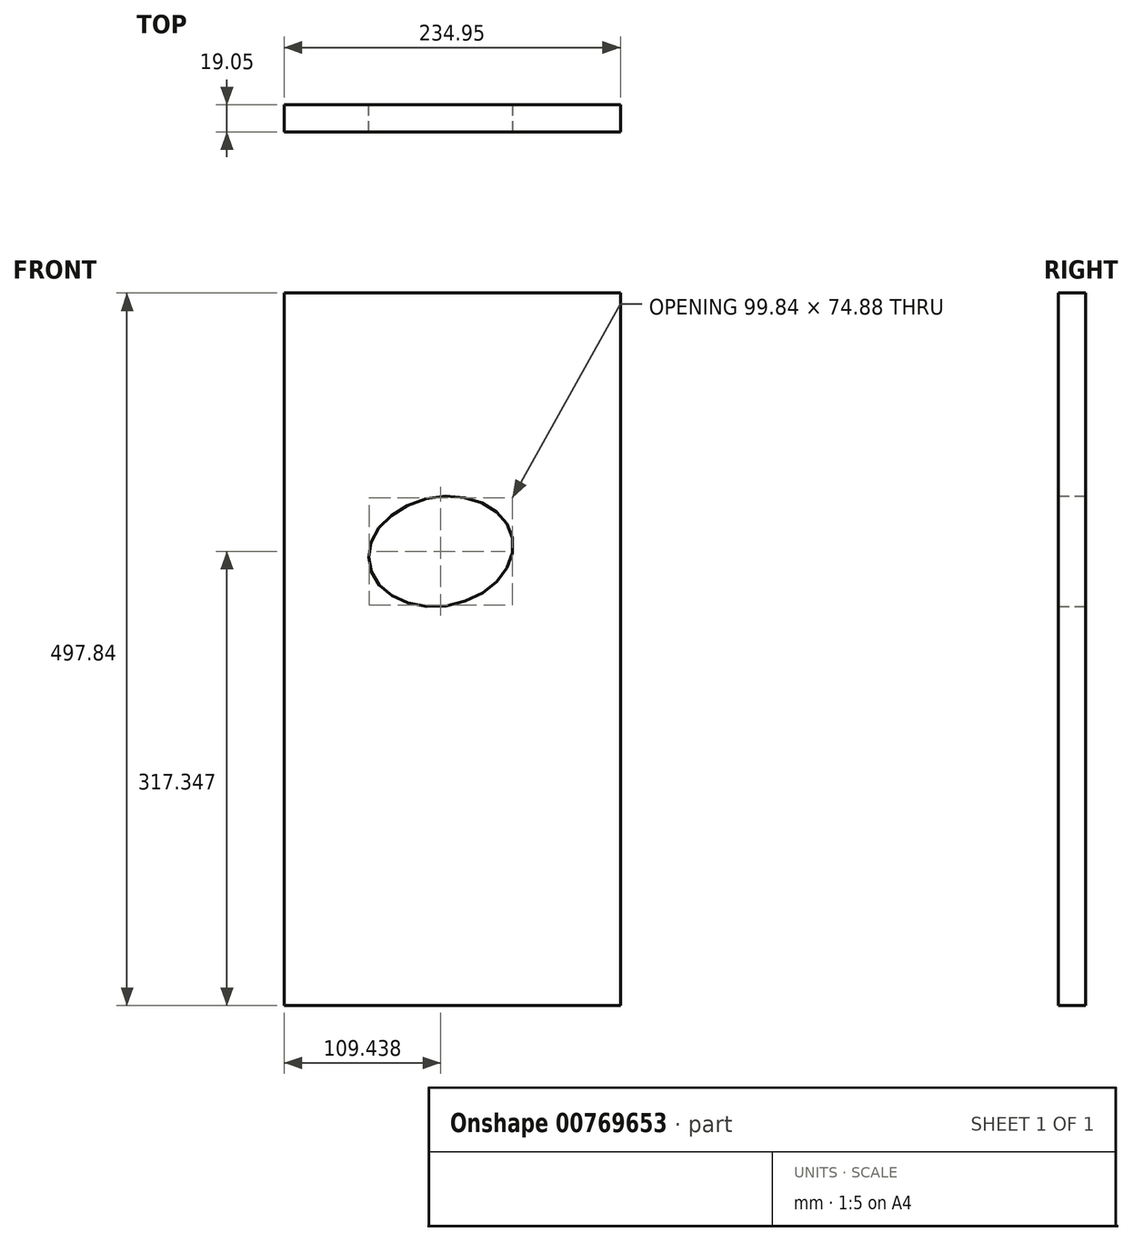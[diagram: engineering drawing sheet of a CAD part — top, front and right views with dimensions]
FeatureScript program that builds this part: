
annotation { "Feature Type Name" : "Feature", "Feature Type Description" : "" }
export const myFeature = defineFeature(function(context is Context, id is Id, definition is map)
    precondition{}
    {
        {
            var Q0;
            Q0=qCreatedBy(makeId("Front.planeOp"),FACE);
            var sketch = newSketch(context, id + "F0", { "sketchPlane" : qUnion([Q0])});
            skLineSegment(sketch, "E0.bottom", {"start": v(-193.54, 428.98) * mm, "end": v(41.41, 428.98) * mm});
            skLineSegment(sketch, "E0.top", {"start": v(-193.54, -68.86) * mm, "end": v(41.41, -68.86) * mm});
            skLineSegment(sketch, "E0.left", {"start": v(-193.54, 428.98) * mm, "end": v(-193.54, -68.86) * mm});
            skLineSegment(sketch, "E0.right", {"start": v(41.41, 428.98) * mm, "end": v(41.41, -68.86) * mm});
            skSolve(sketch);
        }
        {
            var Q0;
            Q0=makeQuery(id+"F0.imprint","IMPRINT",FACE,{"disambiguationData":[TD([[makeQuery(id+"F0.imprint","IMPRINT",EDGE,{"derivedFrom":sQuery(id+"F0.wireOp",EDGE,"E0.bottom")}),-1.0]])]});
            var sketch = newSketch(context, id + "F1", { "sketchPlane" : qUnion([Q0])});
            skEllipse(sketch, "E1", {"center": v(-84.1, 248.49) * mm, "majorRadius": 50.8 * mm, "minorRadius": 38.1 * mm, "majorAxis": v(0.98, 0.19)});
            skSolve(sketch);
        }
        {
            var Q0;
            Q0=makeQuery(id+"F1.imprint","IMPRINT",FACE,{"disambiguationData":[TD([[makeQuery(id+"F1.imprint","IMPRINT",EDGE,{"derivedFrom":sQuery(id+"F1.wireOp",EDGE,"E1")}),-1.0]])]});
            extrude(context, id + "F2", {"entities" : qUnion([Q0]), "depth" : 19.05 * mm, "offsetDistance" : 25.4 * mm});
        }
    });
